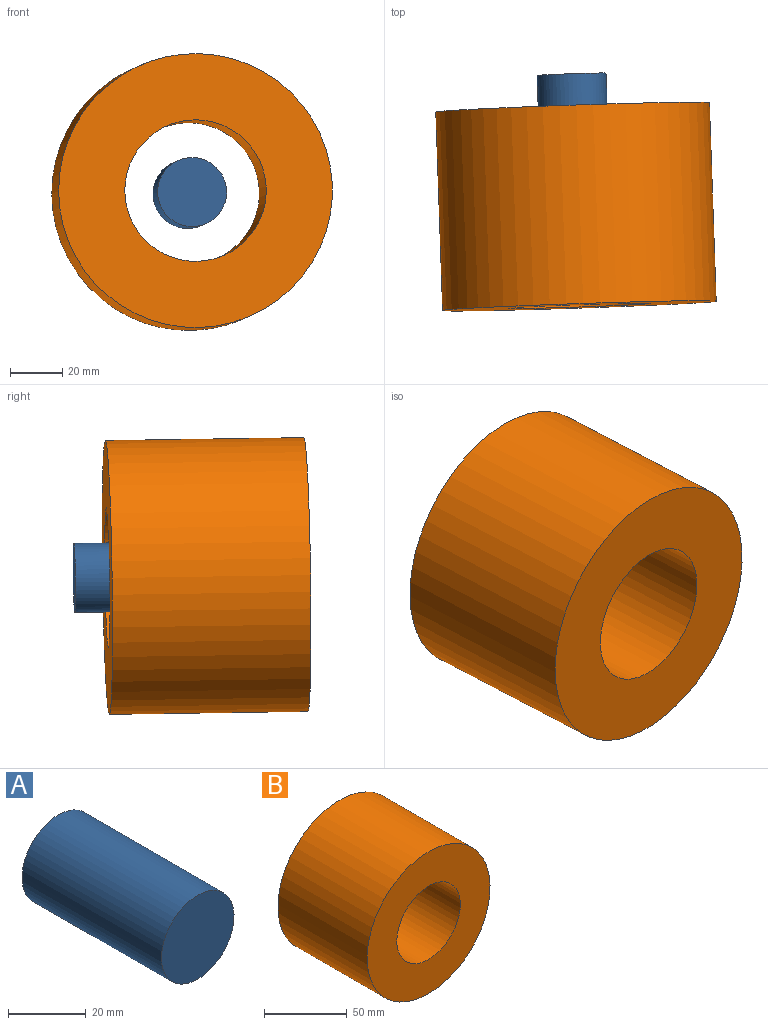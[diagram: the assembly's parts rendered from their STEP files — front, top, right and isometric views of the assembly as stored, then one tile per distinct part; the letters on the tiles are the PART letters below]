
ASSEMBLY  parts=2 mates=1
PART A: 3 faces, bbox 26.5x50.8x26.5 mm
  f0: cylinder r=13.24mm len=50.8mm, axis (0,1,0), area 4224.5mm2, adj f1,f2
  f1: plane 26.47x26.47mm, normal (0,-1,0), area 550.3mm2, adj f0
  f2: plane 26.47x26.47mm, normal (0,1,0), area 550.3mm2, adj f0
PART B: 4 faces, bbox 105.1x76.2x105.1 mm
  f0: cylinder r=27.15mm len=76.2mm, axis (0,1,0), area 12998.4mm2, adj f2,f3
  f1: cylinder r=52.55mm len=105.1mm, axis (0,1,0), area 25159.4mm2, adj f2,f3
  f2: plane 105.1x105.1mm, normal (0,-1,0), area 6359.6mm2, adj f0,f1
  f3: plane 105.1x105.1mm, normal (0,1,0), area 6359.6mm2, adj f0,f1
PLACE A rot(axis=(-0.02,-1,0.09),23.3deg) t=(-36,-20.03,-64.72)mm
PLACE B rot(axis=(-0.02,-1,0.09),23.3deg) t=(-0.03,-43.04,14.56)mm fixed
MATE slider A.f0 <-> B.f1  axis (-0.03,1,-0.01) through (-0.9,-17.66,14.19)mm
